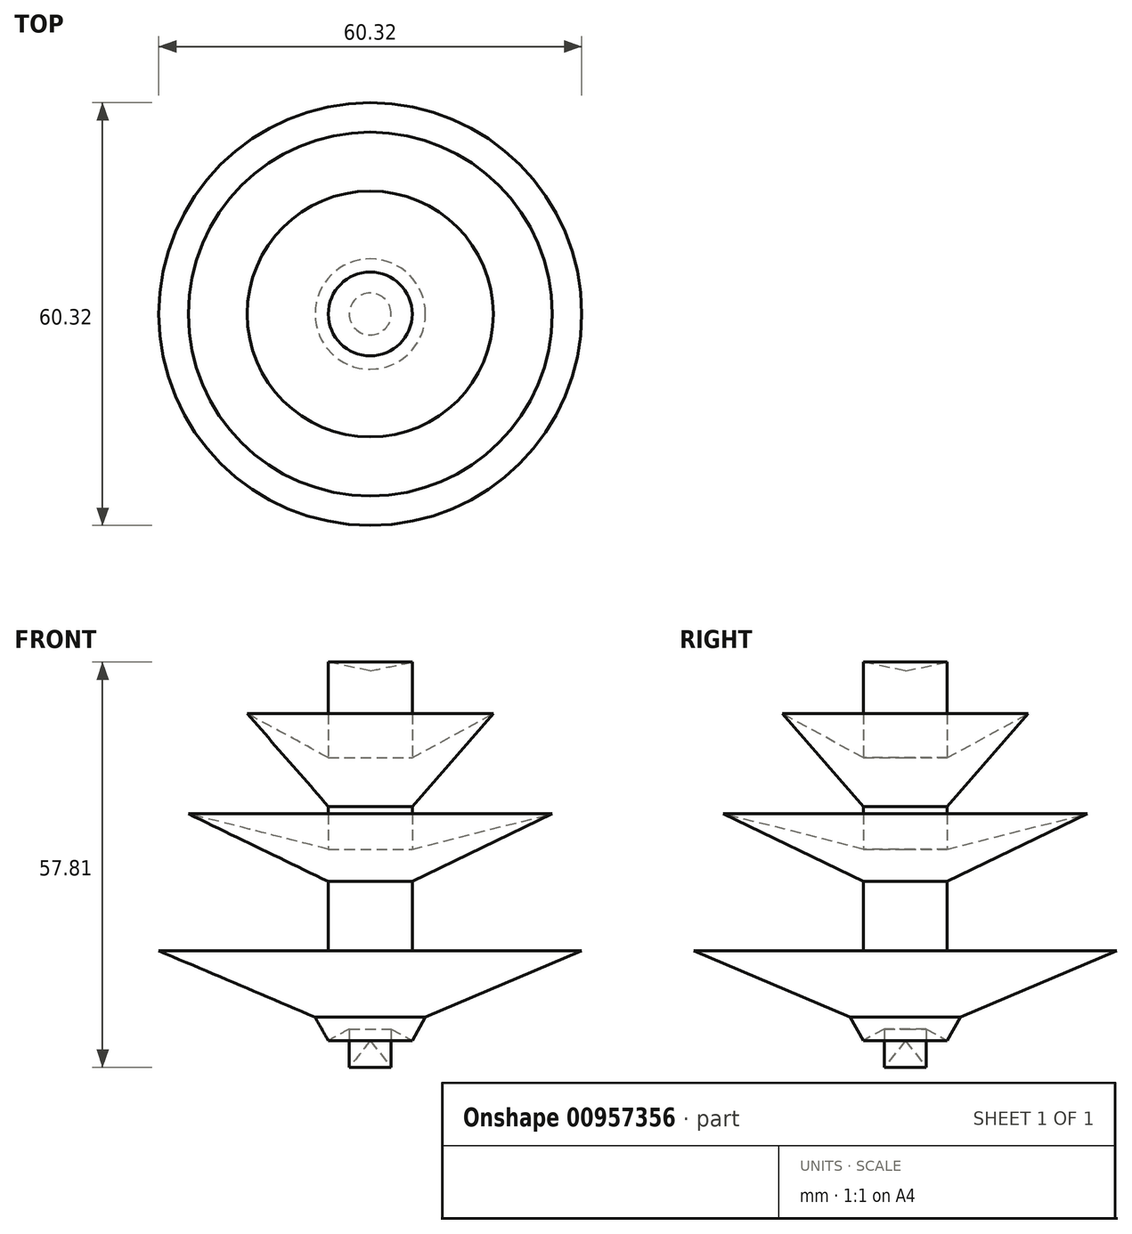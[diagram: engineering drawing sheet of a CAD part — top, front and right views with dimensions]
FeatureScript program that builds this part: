
annotation { "Feature Type Name" : "Feature", "Feature Type Description" : "" }
export const myFeature = defineFeature(function(context is Context, id is Id, definition is map)
    precondition{}
    {
        {
            var Q0;
            Q0=qCreatedBy(makeId("Front.planeOp"),FACE);
            var sketch = newSketch(context, id + "F0", { "sketchPlane" : qUnion([Q0])});
            skLineSegment(sketch, "E0", {"start": v(14.82, 55.92) * mm, "end": v(14.82, 14.72) * mm});
            skLineSegment(sketch, "E1", {"start": v(14.82, 14.72) * mm, "end": v(39, 14.72) * mm});
            skLineSegment(sketch, "E2", {"start": v(39, 14.72) * mm, "end": v(16.71, 5.26) * mm});
            skLineSegment(sketch, "E3", {"start": v(16.71, 5.26) * mm, "end": v(14.82, 1.9) * mm});
            skLineSegment(sketch, "E4", {"start": v(14.82, 1.9) * mm, "end": v(8.84, 5.26) * mm});
            skLineSegment(sketch, "E5", {"start": v(8.84, 5.26) * mm, "end": v(8.84, 54.66) * mm});
            skLineSegment(sketch, "E6", {"start": v(8.84, 54.66) * mm, "end": v(14.82, 55.92) * mm});
            skLineSegment(sketch, "E7", {"start": v(14.82, 55.92) * mm, "end": v(8.84, 55.92) * mm});
            skLineSegment(sketch, "E8", {"start": v(8.84, 5.26) * mm, "end": v(8.84, 1.9) * mm});
            skLineSegment(sketch, "E9", {"start": v(8.84, 1.9) * mm, "end": v(11.83, 3.57) * mm});
            skLineSegment(sketch, "E10", {"start": v(11.83, 3.57) * mm, "end": v(11.83, -1.9) * mm});
            skLineSegment(sketch, "E11", {"start": v(11.83, -1.9) * mm, "end": v(8.84, 1.9) * mm});
            skLineSegment(sketch, "E12", {"start": v(11.83, -3.78) * mm, "end": v(14.82, 1.9) * mm});
            skLineSegment(sketch, "E13", {"start": v(14.82, 35.32) * mm, "end": v(26.39, 48.57) * mm});
            skLineSegment(sketch, "E14", {"start": v(26.39, 48.57) * mm, "end": v(14.82, 42.26) * mm});
            skLineSegment(sketch, "E15", {"start": v(14.82, 42.26) * mm, "end": v(14.82, 24.6) * mm});
            skLineSegment(sketch, "E16", {"start": v(14.82, 24.6) * mm, "end": v(34.8, 34.27) * mm});
            skLineSegment(sketch, "E17", {"start": v(34.8, 34.27) * mm, "end": v(14.82, 29.22) * mm});
            skSolve(sketch);
        }
        {
            var Q0;
            Q0=makeQuery(id+"F0.imprint","IMPRINT",FACE,{"disambiguationData":[TD([[makeQuery(id+"F0.imprint","IMPRINT",EDGE,{"derivedFrom":sQuery(id+"F0.wireOp",EDGE,"E9")}),-1.0]])]});
            var Q1;
            {var subQ0=sQuery(id+"F0.wireOp",EDGE,"E13");Q1=makeQuery(id+"F0.imprint","IMPRINT",FACE,{"disambiguationData":[TD([[makeQuery(id+"F0.imprint","IMPRINT",EDGE,{"derivedFrom":subQ0}),1.0]])]});}
            var Q2;
            {var subQ0=sQuery(id+"F0.wireOp",EDGE,"E16");Q2=makeQuery(id+"F0.imprint","IMPRINT",FACE,{"disambiguationData":[TD([[makeQuery(id+"F0.imprint","IMPRINT",EDGE,{"derivedFrom":subQ0}),1.0]])]});}
            var Q3;
            {var subQ0=sQuery(id+"F0.wireOp",EDGE,"E8");Q3=makeQuery(id+"F0.imprint","IMPRINT",FACE,{"disambiguationData":[TD([[makeQuery(id+"F0.imprint","IMPRINT",EDGE,{"derivedFrom":subQ0}),1.0]])]});}
            var Q4;
            {var subQ9=sQuery(id+"F0.wireOp",EDGE,"E1");Q4=makeQuery(id+"F0.imprint","IMPRINT",FACE,{"disambiguationData":[TD([[makeQuery(id+"F0.imprint","IMPRINT",EDGE,{"derivedFrom":subQ9}),-1.0]])]});}
            var Q5;
            Q5=sQuery(id+"F0.wireOp",EDGE,"E5");
            revolve(context, id + "F1", {"surfaceOperationType" : NewSurfaceOperationType.NEW, "entities" : qUnion([Q0, Q1, Q2, Q3, Q4]), "axis" : qUnion([Q5]), "revolveType" : RevolveType.FULL});
        }
    });
